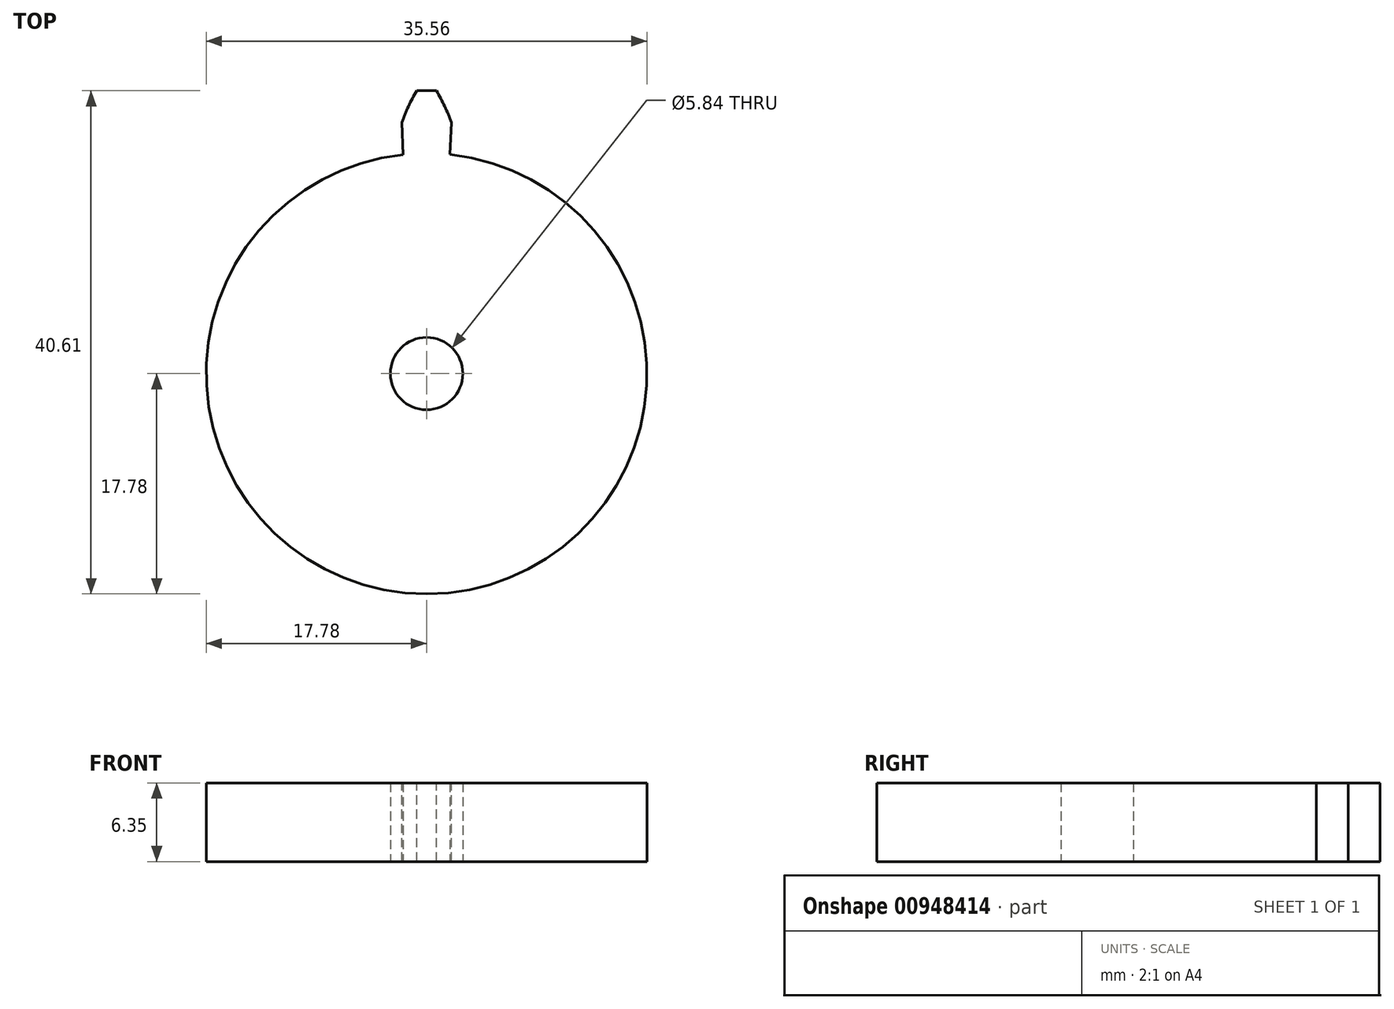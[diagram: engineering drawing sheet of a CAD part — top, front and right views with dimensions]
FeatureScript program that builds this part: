
annotation { "Feature Type Name" : "Feature", "Feature Type Description" : "" }
export const myFeature = defineFeature(function(context is Context, id is Id, definition is map)
    precondition{}
    {
        {
            var Q0;
            Q0=qCreatedBy(makeId("Top.planeOp"),FACE);
            var sketch = newSketch(context, id + "F0", { "sketchPlane" : qUnion([Q0])});
            skCircle(sketch, "E0", {"center": v(0, 0) * mm, "radius": 17.78 * mm});
            skCircle(sketch, "E1", {"center": v(0, 0) * mm, "radius": 2.92 * mm});
            skSolve(sketch);
        }
        {
            var Q0;
            Q0 = qSketchRegion(id + "F0", true);
            extrude(context, id + "F1", {"entities" : qUnion([Q0]), "depth" : 6.35 * mm, "offsetDistance" : 25.4 * mm});
        }
        {
            var Q0;
            Q0=makeQuery(id+"F1.opExtrude","CAP_FACE",FACE,{"disambiguationData":[OSD([sQuery(id+"F0.wireOp",EDGE,"E0"),sQuery(id+"F0.wireOp",EDGE,"E1")])],"isStart":false});
            var sketch = newSketch(context, id + "F2", { "sketchPlane" : qUnion([Q0])});
            skCircle(sketch, "E2", {"center": v(0, 0) * mm, "radius": 20.32 * mm, "construction": true});
            skCircle(sketch, "E3", {"center": v(0, 0) * mm, "radius": 22.86 * mm, "construction": true});
            skLineSegment(sketch, "E4", {"start": v(0, 0) * mm, "end": v(0, 28.9) * mm, "construction": true});
            skLineSegment(sketch, "E5", {"start": v(0, 0) * mm, "end": v(2.84, 28.83) * mm, "construction": true});
            skArc(sketch, "E6.trimOffspring", {"start": v(2, 20.26) * mm, "mid": v(1.46, 21.58) * mm, "end": v(0.8, 22.83) * mm});
            skLineSegment(sketch, "E7", {"start": v(0.8, 22.83) * mm, "end": v(0, 22.83) * mm});
            skLineSegment(sketch, "E8", {"start": v(2, 20.26) * mm, "end": v(1.86, 16.82) * mm});
            skLineSegment(sketch, "E9", {"start": v(1.86, 16.82) * mm, "end": v(0, 16.82) * mm});
            skLineSegment(sketch, "E10.MirrorCS", {"start": v(-0.8, 22.83) * mm, "end": v(0, 22.83) * mm});
            skArc(sketch, "E11.MirrorCS", {"start": v(-2, 20.26) * mm, "mid": v(-1.47, 21.58) * mm, "end": v(-0.8, 22.83) * mm});
            skLineSegment(sketch, "E12.MirrorCS", {"start": v(-2, 20.26) * mm, "end": v(-1.87, 16.82) * mm});
            skLineSegment(sketch, "E13.MirrorCS", {"start": v(-1.87, 16.82) * mm, "end": v(0, 16.82) * mm});
            skSolve(sketch);
        }
        {
            var Q0;
            Q0 = qSketchRegion(id + "F2", true);
            extrude(context, id + "F3", {"entities" : qUnion([Q0]), "operationType" : NewBodyOperationType.ADD, "oppositeDirection" : true, "depth" : 6.35 * mm, "offsetDistance" : 25.4 * mm});
        }
        {
            var Q0;
            Q0=qCreatedBy(makeId("Front.planeOp"),FACE);
            var sketch = newSketch(context, id + "F4", { "sketchPlane" : qUnion([Q0])});
            skLineSegment(sketch, "E14", {"start": v(0, 0) * mm, "end": v(0, 6.36) * mm, "construction": true});
            skSolve(sketch);
        }
    });
